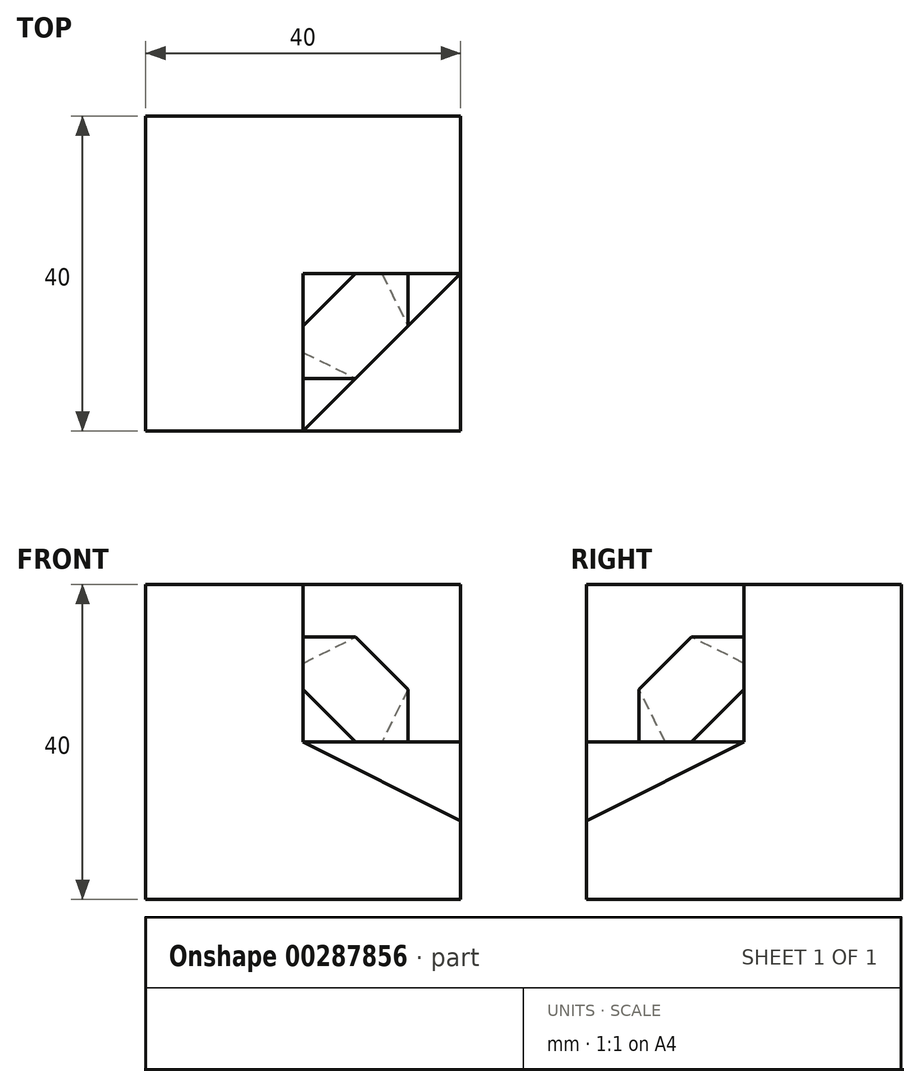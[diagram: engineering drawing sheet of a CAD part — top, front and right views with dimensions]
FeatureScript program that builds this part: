
annotation { "Feature Type Name" : "Feature", "Feature Type Description" : "" }
export const myFeature = defineFeature(function(context is Context, id is Id, definition is map)
    precondition{}
    {
        {
            var Q0;
            Q0=qCreatedBy(makeId("Front.planeOp"),FACE);
            var sketch = newSketch(context, id + "F0", { "sketchPlane" : qUnion([Q0])});
            skLineSegment(sketch, "E0.bottom", {"start": v(0, 0) * mm, "end": v(40, 0) * mm});
            skLineSegment(sketch, "E0.top", {"start": v(0, 40) * mm, "end": v(40, 40) * mm});
            skLineSegment(sketch, "E0.left", {"start": v(0, 0) * mm, "end": v(0, 40) * mm});
            skLineSegment(sketch, "E0.right", {"start": v(40, 0) * mm, "end": v(40, 40) * mm});
            skSolve(sketch);
        }
        {
            var Q0;
            Q0=qSketchRegion(id+"F0",true);
            extrude(context, id + "F1", {"entities" : qUnion([Q0]), "depth" : 40 * mm});
        }
        {
            var Q0;
            Q0=makeQuery(id+"F1.opExtrude","CAP_FACE",FACE,{"disambiguationData":[OSD([sQuery(id+"F0.wireOp",EDGE,"E0.bottom"),sQuery(id+"F0.wireOp",EDGE,"E0.top"),sQuery(id+"F0.wireOp",EDGE,"E0.left"),sQuery(id+"F0.wireOp",EDGE,"E0.right")])],"isStart":false});
            var sketch = newSketch(context, id + "F2", { "sketchPlane" : qUnion([Q0])});
            skPoint(sketch, "E1.oppositeSnap0", {"position": v(20, 0) * mm});
            skPoint(sketch, "E1.oppositeSnap1", {"position": v(0, 20) * mm});
            skLineSegment(sketch, "E1.bottom", {"start": v(40, 40) * mm, "end": v(20, 40) * mm});
            skLineSegment(sketch, "E1.top", {"start": v(40, 20) * mm, "end": v(20, 20) * mm});
            skLineSegment(sketch, "E1.left", {"start": v(40, 40) * mm, "end": v(40, 20) * mm});
            skLineSegment(sketch, "E1.right", {"start": v(20, 40) * mm, "end": v(20, 20) * mm});
            skSolve(sketch);
        }
        {
            var Q0;
            Q0=qSketchRegion(id+"F2",true);
            extrude(context, id + "F3", {"entities" : qUnion([Q0]), "operationType" : NewBodyOperationType.REMOVE, "oppositeDirection" : true, "depth" : 20 * mm});
        }
        {
            var Q0;
            Q0=makeQuery(id+"F1.opExtrude","CAP_EDGE",EDGE,{"disambiguationData":[OSD([sQuery(id+"F0.wireOp",EDGE,"E0.right")])],"isStart":false});
            cPoint(context, id + "F4", {"entities" : qUnion([Q0]), "parameter" : 0.5});
        }
        {
            var Q0;
            Q0=makeQuery(id+"F3.boolean.opBoolean","COPY",VERTEX,{"derivedFrom":makeQuery(id+"F3.opExtrude","CAP_VERTEX",VERTEX,{"disambiguationData":[OSD([sQuery(id+"F0.wireOp",EDGE,"E0.right"),sQuery(id+"F2.wireOp",EDGE,"E1.top"),sQuery(id+"F2.wireOp",EDGE,"E1.left")])],"isStart":false})});
            var Q1;
            Q1=makeQuery(id+"F3.boolean.opBoolean","COPY",VERTEX,{"derivedFrom":makeQuery(id+"F3.opExtrude","CAP_VERTEX",VERTEX,{"disambiguationData":[OSD([sQuery(id+"F2.wireOp",EDGE,"E1.top"),sQuery(id+"F2.wireOp",EDGE,"E1.right")])],"isStart":true})});
            var Q2;
            Q2=qCreatedBy(id+"F4",VERTEX);
            cPlane(context, id + "F5", {"entities" : qUnion([Q0, Q1, Q2]), "cplaneType" : CPlaneType.THREE_POINT, "offset" : 25 * mm, "width" : 150 * mm, "height" : 150 * mm});
        }
        {
            var Q0;
            Q0=qCreatedBy(id+"F5.planeOp",FACE);
            var sketch = newSketch(context, id + "F6", { "sketchPlane" : qUnion([Q0])});
            skPoint(sketch, "E2.0", {"position": v(25.56, 8.94) * mm});
            skPoint(sketch, "E3.0", {"position": v(3.65, 26.83) * mm});
            skPoint(sketch, "E4.0", {"position": v(25.56, 31.3) * mm});
            skLineSegment(sketch, "E5", {"start": v(25.56, 8.94) * mm, "end": v(3.65, 26.83) * mm});
            skLineSegment(sketch, "E6", {"start": v(25.56, 31.3) * mm, "end": v(3.65, 26.83) * mm});
            skLineSegment(sketch, "E7", {"start": v(25.56, 8.94) * mm, "end": v(25.56, 31.3) * mm});
            skSolve(sketch);
        }
        {
            var Q0;
            Q0=qSketchRegion(id+"F6",true);
            extrude(context, id + "F7", {"entities" : qUnion([Q0]), "operationType" : NewBodyOperationType.REMOVE, "endBound" : BoundingType.THROUGH_ALL, "oppositeDirection" : true, "depth" : 25 * mm});
        }
        {
            var Q0;
            Q0=makeQuery(id+"F3.boolean.opBoolean","COPY",VERTEX,{"derivedFrom":makeQuery(id+"F3.opExtrude","CAP_VERTEX",VERTEX,{"disambiguationData":[OSD([sQuery(id+"F0.wireOp",EDGE,"E0.top"),sQuery(id+"F2.wireOp",EDGE,"E1.bottom"),sQuery(id+"F2.wireOp",EDGE,"E1.right")])],"isStart":false})});
            var Q1;
            Q1=makeQuery(id+"F7.boolean.opBoolean","MERGE",VERTEX,{"derivedFrom":[makeQuery(id+"F3.boolean.opBoolean","COPY",VERTEX,{"derivedFrom":makeQuery(id+"F3.opExtrude","CAP_VERTEX",VERTEX,{"disambiguationData":[OSD([sQuery(id+"F2.wireOp",EDGE,"E1.top"),sQuery(id+"F2.wireOp",EDGE,"E1.right")])],"isStart":true})}),makeQuery(id+"F7.opExtrude","CAP_VERTEX",VERTEX,{"disambiguationData":[OSD([sQuery(id+"F6.wireOp",EDGE,"E5"),sQuery(id+"F6.wireOp",EDGE,"E6")])],"isStart":true})]});
            var Q2;
            Q2=makeQuery(id+"F7.boolean.opBoolean","MERGE",VERTEX,{"derivedFrom":[makeQuery(id+"F3.boolean.opBoolean","COPY",VERTEX,{"derivedFrom":makeQuery(id+"F3.opExtrude","CAP_VERTEX",VERTEX,{"disambiguationData":[OSD([sQuery(id+"F0.wireOp",EDGE,"E0.right"),sQuery(id+"F2.wireOp",EDGE,"E1.top"),sQuery(id+"F2.wireOp",EDGE,"E1.left")])],"isStart":false})}),makeQuery(id+"F7.opExtrude","CAP_VERTEX",VERTEX,{"disambiguationData":[OSD([sQuery(id+"F6.wireOp",EDGE,"E5"),sQuery(id+"F6.wireOp",EDGE,"E7")])],"isStart":true})]});
            cPlane(context, id + "F8", {"entities" : qUnion([Q0, Q1, Q2]), "cplaneType" : CPlaneType.THREE_POINT, "offset" : 25 * mm, "width" : 150 * mm, "height" : 150 * mm});
        }
        {
            var Q0;
            Q0=qCreatedBy(id+"F8.planeOp",FACE);
            var sketch = newSketch(context, id + "F9", { "sketchPlane" : qUnion([Q0])});
            skPoint(sketch, "E8.0", {"position": v(-8.16, 14.14) * mm});
            skPoint(sketch, "E9.0", {"position": v(16.33, 0) * mm});
            skPoint(sketch, "E10.0", {"position": v(-8.16, -14.14) * mm});
            skLineSegment(sketch, "E11", {"start": v(-8.16, 14.14) * mm, "end": v(16.33, 0) * mm});
            skLineSegment(sketch, "E12", {"start": v(-8.16, -14.14) * mm, "end": v(-8.16, 14.14) * mm});
            skLineSegment(sketch, "E13.0", {"start": v(-8.16, -14.14) * mm, "end": v(16.33, 0) * mm});
            skSolve(sketch);
        }
        {
            var Q0;
            Q0 = qSketchRegion(id + "F9", true);
            extrude(context, id + "F10", {"entities" : qUnion([Q0]), "operationType" : NewBodyOperationType.ADD, "endBound" : BoundingType.UP_TO_NEXT, "depth" : 25 * mm});
        }
    });
